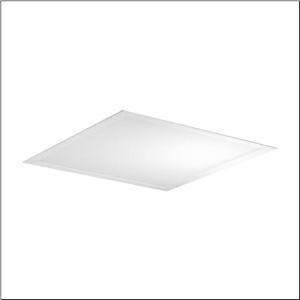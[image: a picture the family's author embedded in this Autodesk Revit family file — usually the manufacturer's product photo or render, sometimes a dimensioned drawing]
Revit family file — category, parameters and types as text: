
# Revit family: apollon_r__31_square_51mp11w72442m_515c
name_source: partatom
category: Lighting Fixtures
units: mm (PartAtom-declared; Revit-internal decimal feet)

## family parameters
Cut with Voids When Loaded = No
Host = Face
Light Source = No
Part Type = Normal
Room Calculation Point = No
Round Connector Dimension = Use Diameter
Shared = No

## types (1)
- Apollon® 31 square (1 x LED, 4000 lm, 27.5 W, 4000K)
    Apparent Load = 28 VA
    CIE Flux Codes = 61 87 97 100 100
    Color Rendering = 80
    Color Temperature = 4000K
    Default Elevation = 1800 mm
    Description = Apollon® 31 square, office luminaire, primary optical cover: micro prismatic cover, of PMMA, CAT 2 (L<= 3000cd/m²), light emission: direct distribution, primary light characteristic: symmetric, installation type: lay-in mounting, LED, rated luminous flux: 4.000lm, luminous efficacy: 145lm/W, light colour: 840, colour temperature: 4000K, with terminal, 3-pole, mains connection: 220..240V, AC, 50/60Hz, rated input power: 28W, housing, of aluminium, traffic white (RAL 9016), module: M625, length: 620mm, width: 620mm, height: 32mm, housing upper side, of sheet steel, galvanised, protection rating (complete): IP20, protection rating (on room side): IP40, insulation class (complete): insulation class II (safety insulation), certification: CE, ENEC, impact resistance: IK03, permissible operating ambient temperature: -20..+40°C, permissible storage temperature: -20..+60°C, packaging unit: set of 6
    Height = 0 mm  [stored 0 ft]
    Lamp = 1 x LED
    Lamp Light Flux = 4000 lm
    Lamp Power = 27.5 W
    Lamp count = 1
    Length = 620 mm
    Luminous efficacy = 145 lm/W
    Manufacturer = Siteco
    ModVariant = No
    Model = 51MP11W72442M
    Mounting Place = Ceiling
    Mounting Type = Recessed
    Number of Poles = 1
    OnlyDefault = Yes
    Power Factor = 1
    Product Name = Apollon® 31 square
    Product group = office luminaire | ceiling recessed
    ProductGroupID = 401
    Protection Class = Protection class II
    Protection Degree = IP 20
    RLX_Detail_Level = 1
    RLX_Emergency_Light_Flux = 0 lm
    RLX_Emergency_Type = 0
    RLX_Emergency_Type_DB = No
    RlxData = <blob elided: 12953 chars, md5=06bc19dc>
    Socket = socket
    Standby Power = 0 W
    System Light Flux = 4000 lm
    System Power = 28 W
    Type Comments = Product without accessories
    Type Image = l_1291039.jpg
    URL = http://relux.com
    VarID = ---
    Voltage = 0 V
    Weight = 0.00 kg
    Width = 620 mm

note: [stored X ft] marks values corroborated as IEEE doubles in the binary element streams (Revit-internal decimal feet)

## geometry (parser evidence)
native form markers: Sweep x9
no freeform markers — native parametric forms only
